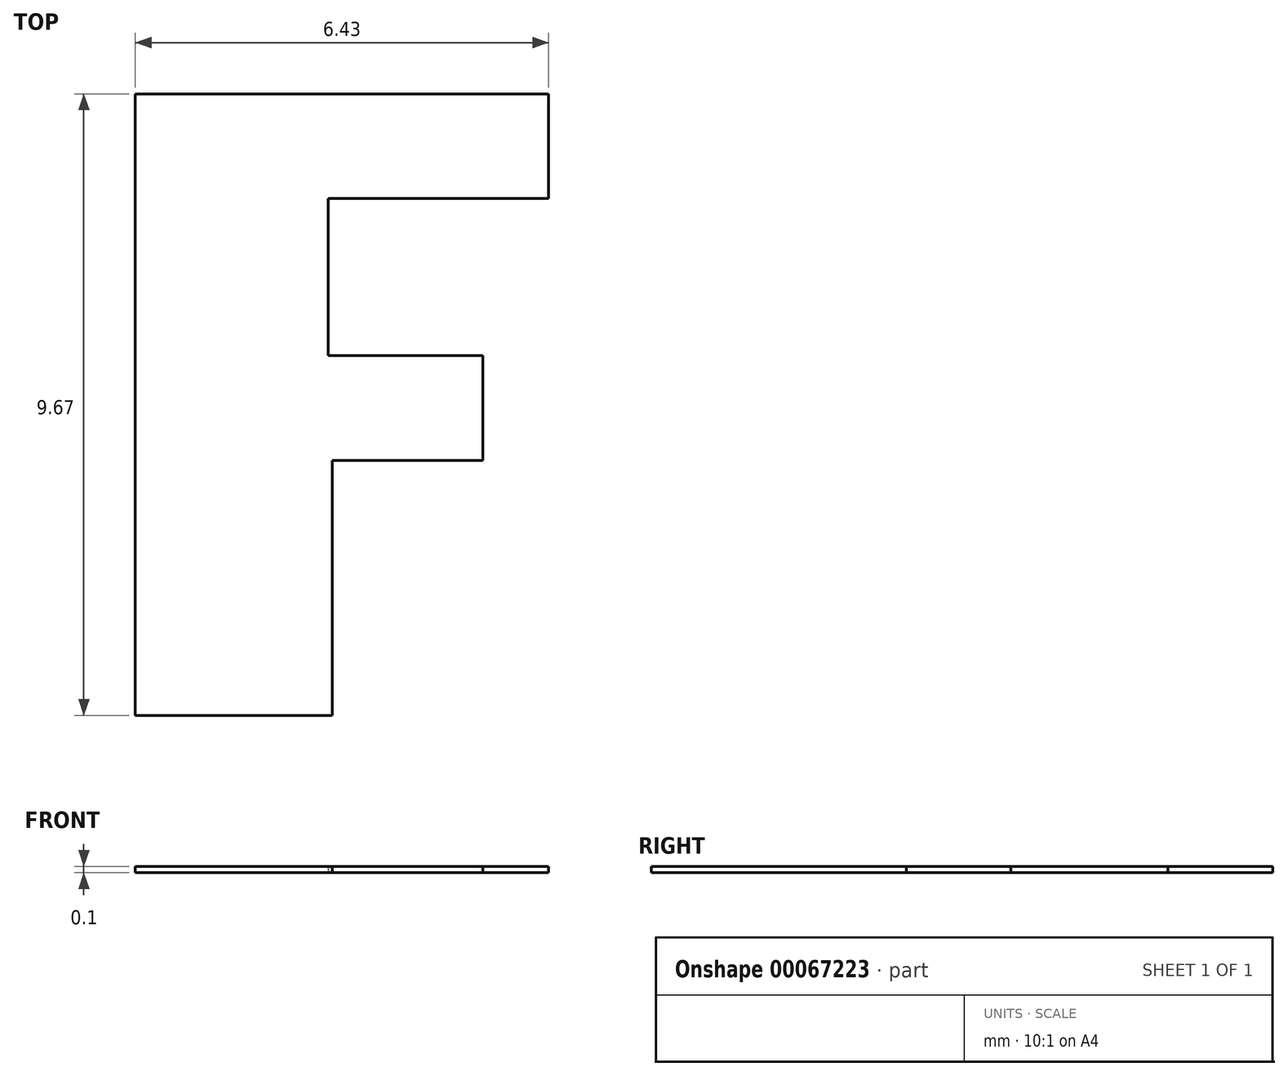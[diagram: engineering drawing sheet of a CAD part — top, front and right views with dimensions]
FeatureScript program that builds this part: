
annotation { "Feature Type Name" : "Feature", "Feature Type Description" : "" }
export const myFeature = defineFeature(function(context is Context, id is Id, definition is map)
    precondition{}
    {
        {
            var Q0;
            Q0=qCreatedBy(makeId("Top.planeOp"),FACE);
            var sketch = newSketch(context, id + "F0", { "sketchPlane" : qUnion([Q0])});
            skLineSegment(sketch, "E0", {"start": v(0, 0) * mm, "end": v(6.43, 0) * mm});
            skLineSegment(sketch, "E1", {"start": v(6.43, 0) * mm, "end": v(6.43, -1.63) * mm});
            skLineSegment(sketch, "E2", {"start": v(6.43, -1.63) * mm, "end": v(3, -1.63) * mm});
            skLineSegment(sketch, "E3", {"start": v(3, -1.63) * mm, "end": v(3, -4.07) * mm});
            skLineSegment(sketch, "E4", {"start": v(3, -4.07) * mm, "end": v(5.4, -4.07) * mm});
            skLineSegment(sketch, "E5", {"start": v(5.4, -4.07) * mm, "end": v(5.4, -5.7) * mm});
            skLineSegment(sketch, "E6", {"start": v(5.4, -5.7) * mm, "end": v(3.07, -5.7) * mm});
            skLineSegment(sketch, "E7", {"start": v(3.07, -5.7) * mm, "end": v(3.07, -9.67) * mm});
            skLineSegment(sketch, "E8", {"start": v(3.07, -9.67) * mm, "end": v(0, -9.67) * mm});
            skLineSegment(sketch, "E9", {"start": v(0, -9.67) * mm, "end": v(0, 0) * mm});
            skSolve(sketch);
        }
        {
            var Q0;
            Q0 = qSketchRegion(id + "F0", true);
            extrude(context, id + "F1", {"entities" : qUnion([Q0]), "depth" : .1 * mm});
        }
    });
